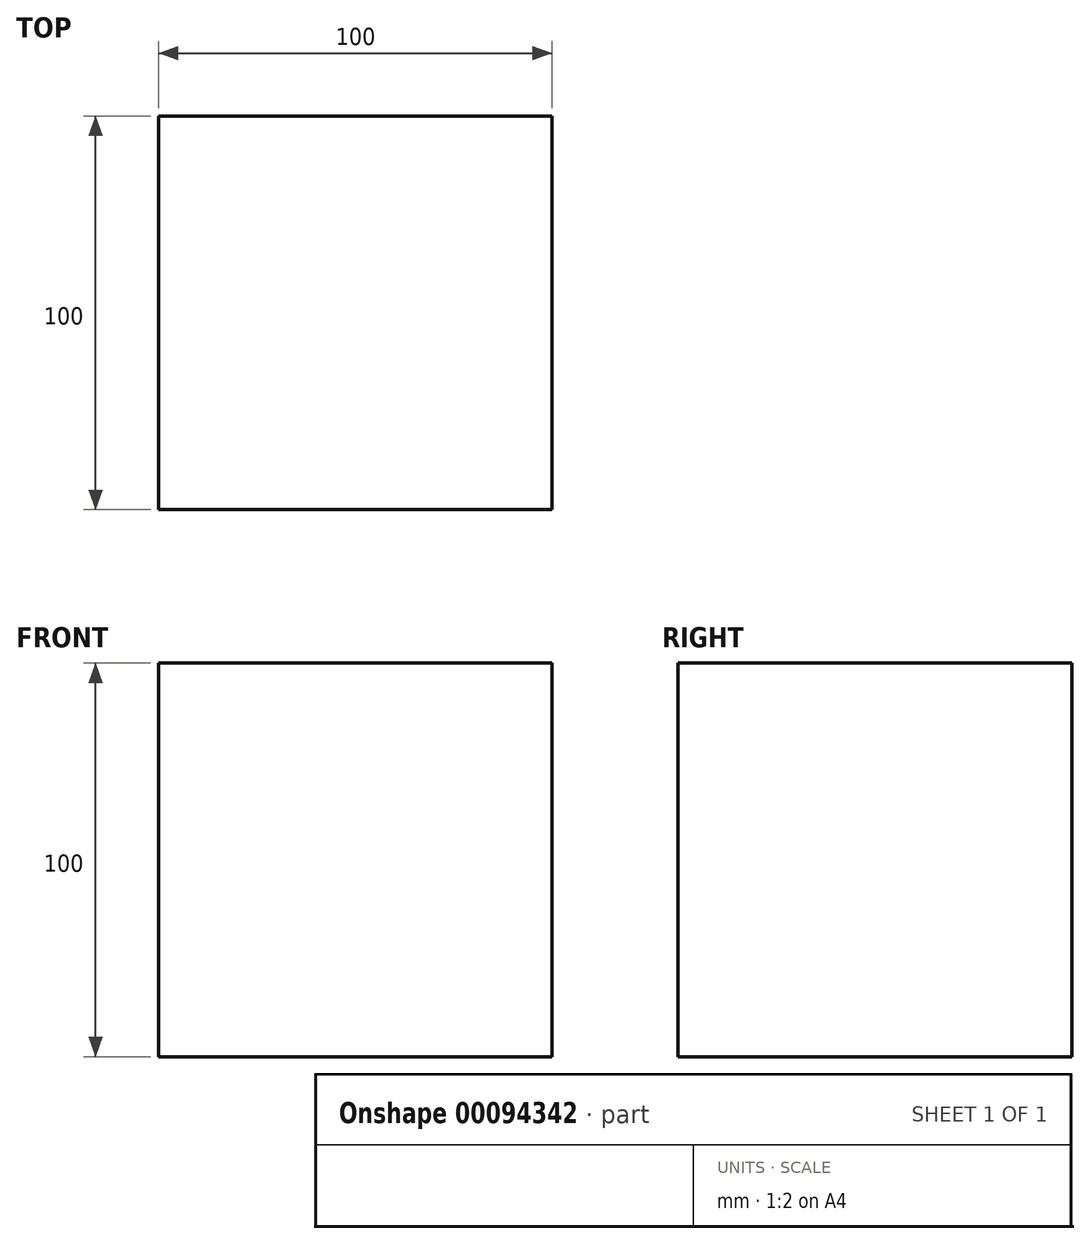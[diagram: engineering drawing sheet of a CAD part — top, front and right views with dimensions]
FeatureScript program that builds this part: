
annotation { "Feature Type Name" : "Feature", "Feature Type Description" : "" }
export const myFeature = defineFeature(function(context is Context, id is Id, definition is map)
    precondition{}
    {
        {
            var Q0;
            Q0=qCreatedBy(makeId("Top.planeOp"),FACE);
            var sketch = newSketch(context, id + "F0", { "sketchPlane" : qUnion([Q0])});
            skLineSegment(sketch, "E0.bottom", {"start": v(50, -50) * mm, "end": v(-50, -50) * mm});
            skLineSegment(sketch, "E0.top", {"start": v(50, 50) * mm, "end": v(-50, 50) * mm});
            skLineSegment(sketch, "E0.left", {"start": v(50, -50) * mm, "end": v(50, 50) * mm});
            skLineSegment(sketch, "E0.right", {"start": v(-50, -50) * mm, "end": v(-50, 50) * mm});
            skPoint(sketch, "E0.middle", {"position": v(0, 0) * mm});
            skSolve(sketch);
        }
        {
            var Q0;
            Q0=makeQuery(id+"F0.imprint","IMPRINT",FACE,{"disambiguationData":[TD([[makeQuery(id+"F0.imprint","IMPRINT",EDGE,{"derivedFrom":sQuery(id+"F0.wireOp",EDGE,"E0.bottom")}),-1.0]])]});
            extrude(context, id + "F1", {"entities" : qUnion([Q0]), "depth" : 100 * mm, "symmetric" : true});
        }
    });
